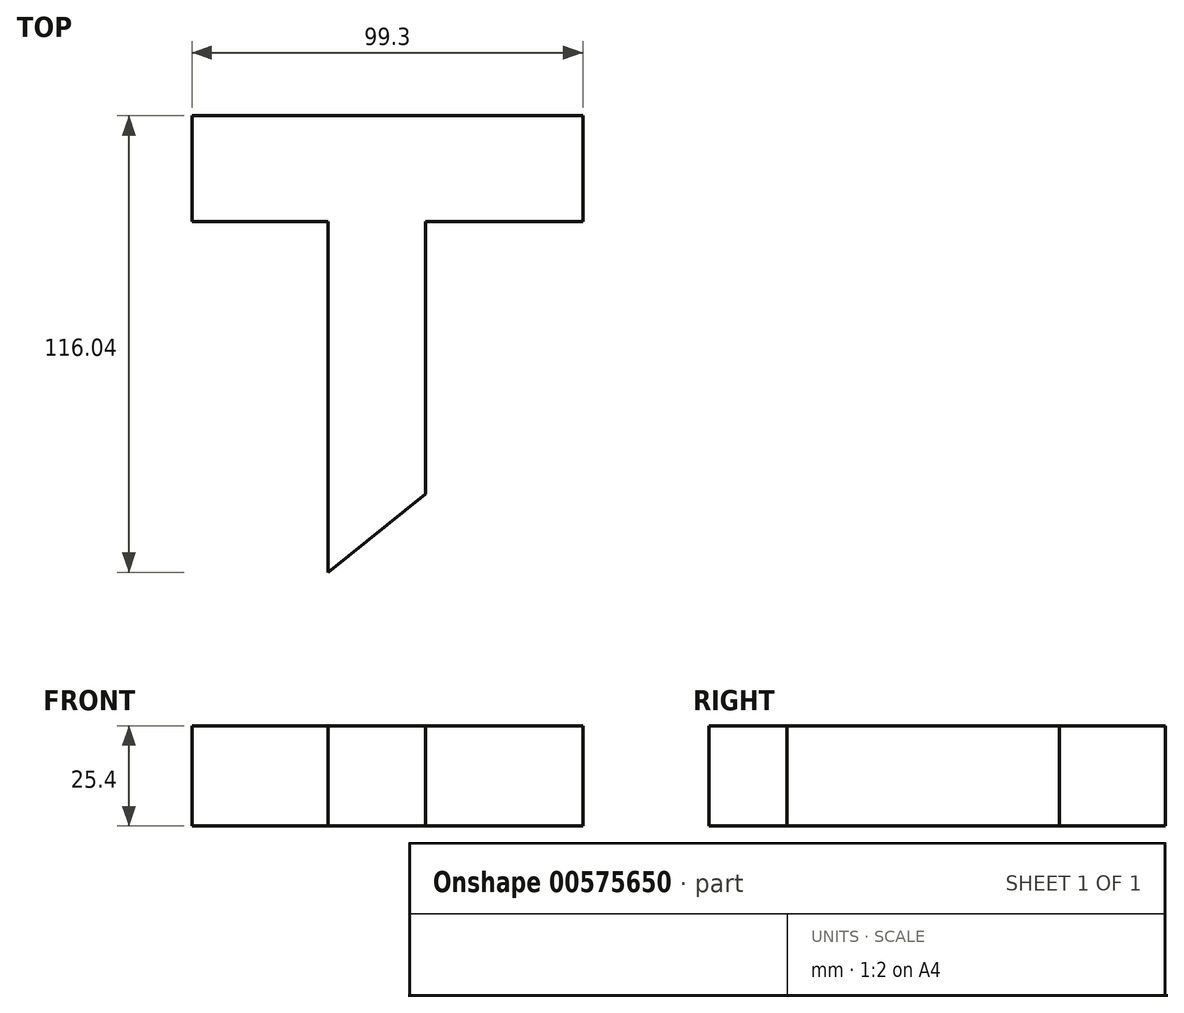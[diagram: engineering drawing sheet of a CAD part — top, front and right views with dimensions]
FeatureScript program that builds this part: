
annotation { "Feature Type Name" : "Feature", "Feature Type Description" : "" }
export const myFeature = defineFeature(function(context is Context, id is Id, definition is map)
    precondition{}
    {
        {
            var Q0;
            Q0=qCreatedBy(makeId("Top.planeOp"),FACE);
            var sketch = newSketch(context, id + "F0", { "sketchPlane" : qUnion([Q0])});
            skLineSegment(sketch, "E0", {"start": v(-51.07, 55.04) * mm, "end": v(-51.07, 42.27) * mm});
            skLineSegment(sketch, "E1", {"start": v(-51.07, 55.04) * mm, "end": v(48.23, 55.04) * mm});
            skLineSegment(sketch, "E2", {"start": v(48.23, 55.04) * mm, "end": v(48.23, 41.7) * mm});
            skLineSegment(sketch, "E3", {"start": v(48.23, 41.7) * mm, "end": v(48.23, 28.09) * mm});
            skLineSegment(sketch, "E4", {"start": v(-51.07, 42.27) * mm, "end": v(-51.07, 28.09) * mm});
            skLineSegment(sketch, "E5", {"start": v(-51.07, 28.09) * mm, "end": v(-16.46, 28.09) * mm});
            skLineSegment(sketch, "E6", {"start": v(48.23, 28.09) * mm, "end": v(8.23, 28.09) * mm});
            skLineSegment(sketch, "E7", {"start": v(-31.2, 28.09) * mm, "end": v(-16.46, 28.09) * mm});
            skLineSegment(sketch, "E8", {"start": v(-16.46, 28.09) * mm, "end": v(-16.46, -61) * mm});
            skLineSegment(sketch, "E9", {"start": v(8.23, 28.09) * mm, "end": v(8.23, -41.14) * mm});
            skLineSegment(sketch, "E10", {"start": v(8.23, -41.14) * mm, "end": v(-16.46, -61) * mm});
            skSolve(sketch);
        }
        {
            var Q0;
            Q0 = qSketchRegion(id + "F0", true);
            extrude(context, id + "F1", {"entities" : qUnion([Q0]), "depth" : 25.4 * mm, "offsetDistance" : 25.4 * mm});
        }
    });
